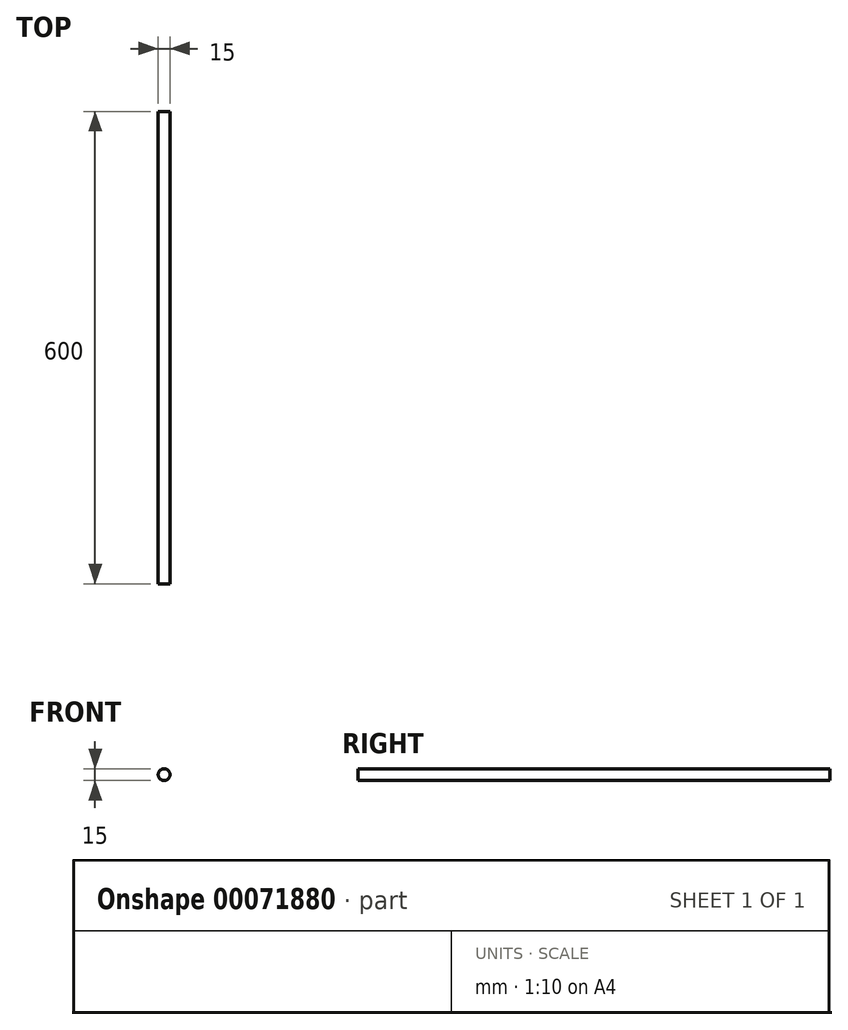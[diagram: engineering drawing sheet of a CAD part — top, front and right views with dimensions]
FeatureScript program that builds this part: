
annotation { "Feature Type Name" : "Feature", "Feature Type Description" : "" }
export const myFeature = defineFeature(function(context is Context, id is Id, definition is map)
    precondition{}
    {
        {
            var Q0;
            Q0=qCreatedBy(makeId("Front.planeOp"),FACE);
            var sketch = newSketch(context, id + "F0", { "sketchPlane" : qUnion([Q0])});
            skCircle(sketch, "E0", {"center": v(0, 0) * mm, "radius": 7.5 * mm});
            skSolve(sketch);
        }
        {
            var Q0;
            Q0 = qSketchRegion(id + "F0", true);
            extrude(context, id + "F1", {"entities" : qUnion([Q0]), "oppositeDirection" : true, "depth" : 600 * mm});
        }
    });
